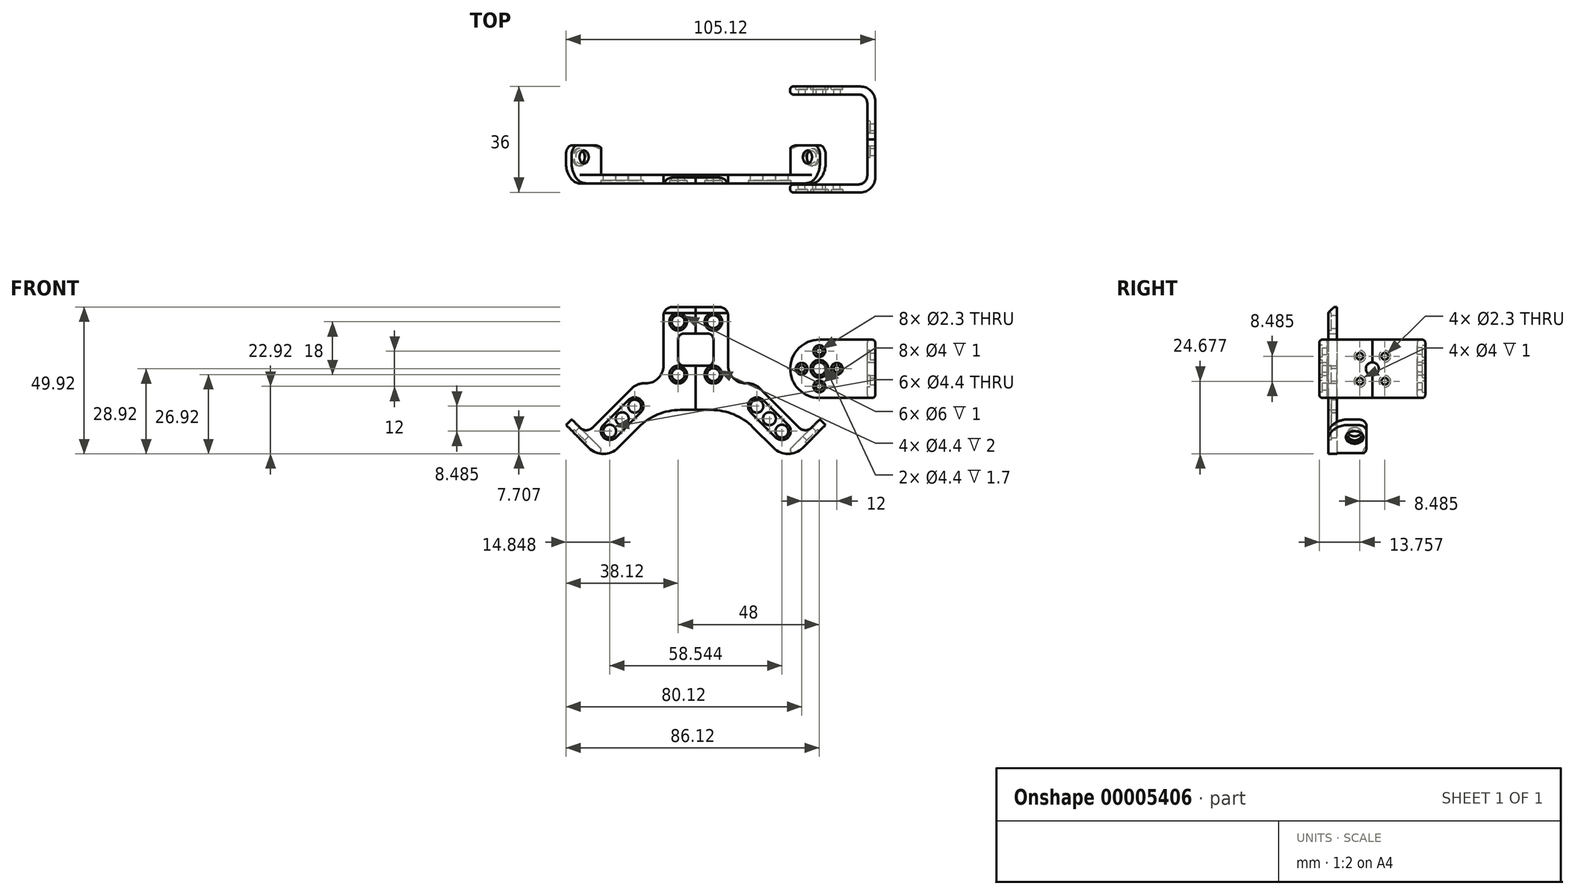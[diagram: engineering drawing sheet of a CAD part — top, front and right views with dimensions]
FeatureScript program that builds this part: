
annotation { "Feature Type Name" : "Feature", "Feature Type Description" : "" }
export const myFeature = defineFeature(function(context is Context, id is Id, definition is map)
    precondition{}
    {
        {
            var Q0;
            Q0=qCreatedBy(makeId("Front.planeOp"),FACE);
            var sketch = newSketch(context, id + "F0", { "sketchPlane" : qUnion([Q0])});
            skLineSegment(sketch, "E0", {"start": v(0, 210) * mm, "end": v(0, -40) * mm});
            skLineSegment(sketch, "E1", {"start": v(-61, 175) * mm, "end": v(61, 175) * mm});
            skPoint(sketch, "E2", {"position": v(0, 175) * mm});
            skLineSegment(sketch, "E3", {"start": v(0, 210) * mm, "end": v(0, 250) * mm});
            skLineSegment(sketch, "E4", {"start": v(-64.02, -38) * mm, "end": v(64.02, -38) * mm});
            skPoint(sketch, "E5", {"position": v(0, -38) * mm});
            skLineSegment(sketch, "E6", {"start": v(44.7, -38) * mm, "end": v(44.7, -100) * mm});
            skLineSegment(sketch, "E7", {"start": v(-51.1, 0) * mm, "end": v(47, 0) * mm});
            skSolve(sketch);
        }
        {
            var Q0;
            Q0=qCreatedBy(makeId("Front.planeOp"),FACE);
            var sketch = newSketch(context, id + "F1", { "sketchPlane" : qUnion([Q0])});
            skLineSegment(sketch, "E8.bottom", {"start": v(64, 184) * mm, "end": v(88, 184) * mm});
            skLineSegment(sketch, "E8.top", {"start": v(64, 148) * mm, "end": v(88, 148) * mm});
            skLineSegment(sketch, "E8.left", {"start": v(64, 184) * mm, "end": v(64, 148) * mm});
            skLineSegment(sketch, "E8.right", {"start": v(88, 184) * mm, "end": v(88, 148) * mm});
            skLineSegment(sketch, "E9", {"start": v(64, 183.9) * mm, "end": v(61, 183.9) * mm});
            skLineSegment(sketch, "E10", {"start": v(61, 183.9) * mm, "end": v(61, 166.1) * mm});
            skLineSegment(sketch, "E11", {"start": v(61, 166.1) * mm, "end": v(64, 166.1) * mm});
            skLineSegment(sketch, "E12", {"start": v(61, 175) * mm, "end": v(88, 175) * mm, "construction": true});
            skCircle(sketch, "E13", {"center": v(42, 175) * mm, "radius": 8.9 * mm});
            skLineSegment(sketch, "E14", {"start": v(14.42, 164.4) * mm, "end": v(39.88, 189.85) * mm});
            skLineSegment(sketch, "E15", {"start": v(39.88, 189.85) * mm, "end": v(56.85, 172.88) * mm});
            skLineSegment(sketch, "E16", {"start": v(56.85, 172.88) * mm, "end": v(31.4, 147.42) * mm});
            skLineSegment(sketch, "E17", {"start": v(31.4, 147.42) * mm, "end": v(14.42, 164.4) * mm});
            skLineSegment(sketch, "E18", {"start": v(33.51, 183.49) * mm, "end": v(50.49, 166.51) * mm, "construction": true});
            skLineSegment(sketch, "E19", {"start": v(48.36, 181.36) * mm, "end": v(22.9, 155.9) * mm, "construction": true});
            skLineSegment(sketch, "E20", {"start": v(2, 0) * mm, "end": v(2, 10) * mm});
            skLineSegment(sketch, "E21", {"start": v(2, 10) * mm, "end": v(5, 10) * mm});
            skLineSegment(sketch, "E22", {"start": v(5, 10) * mm, "end": v(5, 16) * mm});
            skLineSegment(sketch, "E23", {"start": v(5, 16) * mm, "end": v(10, 16) * mm});
            skLineSegment(sketch, "E24", {"start": v(10, 16) * mm, "end": v(10, 10) * mm});
            skLineSegment(sketch, "E25", {"start": v(10, 10) * mm, "end": v(21, 10) * mm});
            skLineSegment(sketch, "E26", {"start": v(21, 10) * mm, "end": v(21, 0) * mm, "construction": true});
            skLineSegment(sketch, "E27", {"start": v(21, 0) * mm, "end": v(2, 0) * mm, "construction": true});
            skLineSegment(sketch, "E28.0.MirrorCS", {"start": v(32, 10) * mm, "end": v(21, 10) * mm});
            skLineSegment(sketch, "E29.0.MirrorCS", {"start": v(32, 16) * mm, "end": v(32, 10) * mm});
            skLineSegment(sketch, "E30.0.MirrorCS", {"start": v(37, 16) * mm, "end": v(32, 16) * mm});
            skLineSegment(sketch, "E31.0.MirrorCS", {"start": v(37, 10) * mm, "end": v(37, 16) * mm});
            skLineSegment(sketch, "E32.0.MirrorCS", {"start": v(40, 10) * mm, "end": v(37, 10) * mm});
            skLineSegment(sketch, "E33.0.MirrorCS", {"start": v(40, 0) * mm, "end": v(40, 10) * mm});
            skLineSegment(sketch, "E34.0.MirrorCS", {"start": v(2, 0) * mm, "end": v(2, -10) * mm});
            skLineSegment(sketch, "E35.0.MirrorCS", {"start": v(2, -10) * mm, "end": v(5, -10) * mm});
            skLineSegment(sketch, "E36.0.MirrorCS", {"start": v(5, -10) * mm, "end": v(5, -16) * mm});
            skLineSegment(sketch, "E37.0.MirrorCS", {"start": v(5, -16) * mm, "end": v(10, -16) * mm});
            skLineSegment(sketch, "E38.0.MirrorCS", {"start": v(10, -16) * mm, "end": v(10, -10) * mm});
            skLineSegment(sketch, "E39.0.MirrorCS", {"start": v(10, -10) * mm, "end": v(21, -10) * mm});
            skLineSegment(sketch, "E40.0.MirrorCS", {"start": v(32, -10) * mm, "end": v(21, -10) * mm});
            skLineSegment(sketch, "E41.0.MirrorCS", {"start": v(32, -16) * mm, "end": v(32, -10) * mm});
            skLineSegment(sketch, "E42.0.MirrorCS", {"start": v(37, -16) * mm, "end": v(32, -16) * mm});
            skLineSegment(sketch, "E43.0.MirrorCS", {"start": v(37, -10) * mm, "end": v(37, -16) * mm});
            skLineSegment(sketch, "E44.0.MirrorCS", {"start": v(40, -10) * mm, "end": v(37, -10) * mm});
            skLineSegment(sketch, "E45.0.MirrorCS", {"start": v(40, 0) * mm, "end": v(40, -10) * mm});
            skLineSegment(sketch, "E46.0.MirrorCS", {"start": v(-2, -10) * mm, "end": v(-5, -10) * mm});
            skLineSegment(sketch, "E46.1.MirrorCS", {"start": v(-10, 10) * mm, "end": v(-21, 10) * mm});
            skLineSegment(sketch, "E46.2.MirrorCS", {"start": v(-32, -16) * mm, "end": v(-32, -10) * mm});
            skLineSegment(sketch, "E46.3.MirrorCS", {"start": v(-37, 10) * mm, "end": v(-37, 16) * mm});
            skLineSegment(sketch, "E46.4.MirrorCS", {"start": v(-5, -10) * mm, "end": v(-5, -16) * mm});
            skLineSegment(sketch, "E46.5.MirrorCS", {"start": v(-40, -10) * mm, "end": v(-37, -10) * mm});
            skLineSegment(sketch, "E46.6.MirrorCS", {"start": v(-32, 10) * mm, "end": v(-21, 10) * mm});
            skLineSegment(sketch, "E46.7.MirrorCS", {"start": v(-2, 0) * mm, "end": v(-2, 10) * mm});
            skLineSegment(sketch, "E46.8.MirrorCS", {"start": v(-10, -10) * mm, "end": v(-21, -10) * mm});
            skLineSegment(sketch, "E46.9.MirrorCS", {"start": v(-5, 16) * mm, "end": v(-10, 16) * mm});
            skLineSegment(sketch, "E46.10.MirrorCS", {"start": v(-5, 10) * mm, "end": v(-5, 16) * mm});
            skLineSegment(sketch, "E46.11.MirrorCS", {"start": v(-10, -16) * mm, "end": v(-10, -10) * mm});
            skLineSegment(sketch, "E46.12.MirrorCS", {"start": v(-37, -10) * mm, "end": v(-37, -16) * mm});
            skLineSegment(sketch, "E46.13.MirrorCS", {"start": v(-40, 0) * mm, "end": v(-40, 10) * mm});
            skLineSegment(sketch, "E46.14.MirrorCS", {"start": v(-40, 10) * mm, "end": v(-37, 10) * mm});
            skLineSegment(sketch, "E46.15.MirrorCS", {"start": v(-21, 0) * mm, "end": v(-2, 0) * mm, "construction": true});
            skLineSegment(sketch, "E46.16.MirrorCS", {"start": v(-10, 16) * mm, "end": v(-10, 10) * mm});
            skLineSegment(sketch, "E46.17.MirrorCS", {"start": v(-2, 0) * mm, "end": v(-2, -10) * mm});
            skLineSegment(sketch, "E46.18.MirrorCS", {"start": v(-32, -10) * mm, "end": v(-21, -10) * mm});
            skLineSegment(sketch, "E46.19.MirrorCS", {"start": v(-37, -16) * mm, "end": v(-32, -16) * mm});
            skLineSegment(sketch, "E46.20.MirrorCS", {"start": v(-37, 16) * mm, "end": v(-32, 16) * mm});
            skLineSegment(sketch, "E46.21.MirrorCS", {"start": v(-2, 10) * mm, "end": v(-5, 10) * mm});
            skLineSegment(sketch, "E46.22.MirrorCS", {"start": v(-5, -16) * mm, "end": v(-10, -16) * mm});
            skLineSegment(sketch, "E46.23.MirrorCS", {"start": v(-32, 16) * mm, "end": v(-32, 10) * mm});
            skLineSegment(sketch, "E46.24.MirrorCS", {"start": v(-40, 0) * mm, "end": v(-40, -10) * mm});
            skLineSegment(sketch, "E46.25.MirrorCS", {"start": v(-21, 10) * mm, "end": v(-21, 0) * mm, "construction": true});
            skLineSegment(sketch, "E47.rect.bottom", {"start": v(42.5, 26.5) * mm, "end": v(-42.5, 26.5) * mm});
            skLineSegment(sketch, "E47.rect.top", {"start": v(42.5, 63.5) * mm, "end": v(-42.5, 63.5) * mm});
            skLineSegment(sketch, "E47.rect.left", {"start": v(42.5, 26.5) * mm, "end": v(42.5, 63.5) * mm});
            skLineSegment(sketch, "E47.rect.right", {"start": v(-42.5, 26.5) * mm, "end": v(-42.5, 63.5) * mm});
            skPoint(sketch, "E47.rect.middle", {"position": v(0, 45) * mm});
            skLineSegment(sketch, "E48.rect.bottom", {"start": v(12, 213) * mm, "end": v(-12, 213) * mm});
            skLineSegment(sketch, "E48.rect.top", {"start": v(12, 237) * mm, "end": v(-12, 237) * mm});
            skLineSegment(sketch, "E48.rect.left", {"start": v(12, 213) * mm, "end": v(12, 237) * mm});
            skLineSegment(sketch, "E48.rect.right", {"start": v(-12, 213) * mm, "end": v(-12, 237) * mm});
            skPoint(sketch, "E48.rect.middle", {"position": v(0, 225) * mm});
            skLineSegment(sketch, "E49", {"start": v(-8.9, 213) * mm, "end": v(-8.9, 210) * mm});
            skLineSegment(sketch, "E50", {"start": v(-8.9, 210) * mm, "end": v(8.9, 210) * mm});
            skLineSegment(sketch, "E51", {"start": v(8.9, 210) * mm, "end": v(8.9, 213) * mm});
            skLineSegment(sketch, "E52.rect.bottom", {"start": v(-12, 200) * mm, "end": v(12, 200) * mm});
            skLineSegment(sketch, "E52.rect.top", {"start": v(-12, 164) * mm, "end": v(12, 164) * mm});
            skLineSegment(sketch, "E52.rect.left", {"start": v(-12, 200) * mm, "end": v(-12, 164) * mm});
            skLineSegment(sketch, "E52.rect.right", {"start": v(12, 200) * mm, "end": v(12, 164) * mm});
            skPoint(sketch, "E52.rect.middle", {"position": v(0, 182) * mm});
            skLineSegment(sketch, "E53.rect.bottom", {"start": v(15, 182.1) * mm, "end": v(-15, 182.1) * mm});
            skLineSegment(sketch, "E53.rect.top", {"start": v(15, 199.9) * mm, "end": v(-15, 199.9) * mm});
            skLineSegment(sketch, "E53.rect.left", {"start": v(15, 182.1) * mm, "end": v(15, 199.9) * mm});
            skLineSegment(sketch, "E53.rect.right", {"start": v(-15, 182.1) * mm, "end": v(-15, 199.9) * mm});
            skPoint(sketch, "E53.rect.middle", {"position": v(0, 191) * mm});
            skCircle(sketch, "E54", {"center": v(42, 175) * mm, "radius": 15 * mm, "construction": true});
            skCircle(sketch, "E55", {"center": v(42, 175) * mm, "radius": 6 * mm, "construction": true});
            skCircle(sketch, "E56", {"center": v(46.24, 179.24) * mm, "radius": 2.5 * mm, "construction": true});
            skCircle(sketch, "E57", {"center": v(37.76, 179.24) * mm, "radius": 2.5 * mm, "construction": true});
            skCircle(sketch, "E58", {"center": v(37.76, 170.76) * mm, "radius": 2.5 * mm, "construction": true});
            skCircle(sketch, "E59", {"center": v(46.24, 170.76) * mm, "radius": 2.5 * mm, "construction": true});
            skLineSegment(sketch, "E60", {"start": v(42, 181) * mm, "end": v(42, 169) * mm, "construction": true});
            skLineSegment(sketch, "E61", {"start": v(48, 175) * mm, "end": v(36, 175) * mm, "construction": true});
            skCircle(sketch, "E62", {"center": v(42, 181) * mm, "radius": 0.8 * mm});
            skCircle(sketch, "E63", {"center": v(48, 175) * mm, "radius": 0.8 * mm});
            skCircle(sketch, "E64", {"center": v(42, 169) * mm, "radius": 0.8 * mm});
            skCircle(sketch, "E65", {"center": v(36, 175) * mm, "radius": 0.8 * mm});
            skLineSegment(sketch, "E66", {"start": v(-6, 191) * mm, "end": v(6, 191) * mm, "construction": true});
            skLineSegment(sketch, "E67", {"start": v(-6, 173) * mm, "end": v(6, 173) * mm, "construction": true});
            skCircle(sketch, "E68", {"center": v(-6, 191) * mm, "radius": 2.5 * mm});
            skCircle(sketch, "E69", {"center": v(0, 191) * mm, "radius": 2.5 * mm});
            skCircle(sketch, "E70", {"center": v(6, 191) * mm, "radius": 2.5 * mm});
            skCircle(sketch, "E71", {"center": v(-6, 173) * mm, "radius": 2.5 * mm});
            skCircle(sketch, "E72", {"center": v(0, 173) * mm, "radius": 2.5 * mm});
            skCircle(sketch, "E73", {"center": v(6, 173) * mm, "radius": 2.5 * mm});
            skLineSegment(sketch, "E74", {"start": v(20.79, 162.27) * mm, "end": v(29.27, 153.79) * mm, "construction": true});
            skCircle(sketch, "E75", {"center": v(29.27, 153.79) * mm, "radius": 2.5 * mm, "construction": true});
            skCircle(sketch, "E76", {"center": v(20.79, 162.27) * mm, "radius": 2.5 * mm, "construction": true});
            skCircle(sketch, "E77", {"center": v(25.03, 158.03) * mm, "radius": 2.5 * mm, "construction": true});
            skLineSegment(sketch, "E78.rect.bottom", {"start": v(12, 81.5) * mm, "end": v(-12, 81.5) * mm});
            skLineSegment(sketch, "E78.rect.top", {"start": v(12, 105.5) * mm, "end": v(-12, 105.5) * mm});
            skLineSegment(sketch, "E78.rect.left", {"start": v(12, 81.5) * mm, "end": v(12, 105.5) * mm});
            skLineSegment(sketch, "E78.rect.right", {"start": v(-12, 81.5) * mm, "end": v(-12, 105.5) * mm});
            skPoint(sketch, "E78.rect.middle", {"position": v(0, 93.5) * mm});
            skLineSegment(sketch, "E79", {"start": v(-8.9, 81.5) * mm, "end": v(-8.9, 78.5) * mm});
            skLineSegment(sketch, "E80", {"start": v(-8.9, 78.5) * mm, "end": v(8.9, 78.5) * mm});
            skLineSegment(sketch, "E81", {"start": v(8.9, 78.5) * mm, "end": v(8.9, 81.5) * mm});
            skLineSegment(sketch, "E82", {"start": v(0, 93.5) * mm, "end": v(0, 78.5) * mm, "construction": true});
            skCircle(sketch, "E83", {"center": v(42, 175) * mm, "radius": 2.5 * mm});
            skSolve(sketch);
        }
        {
            var Q0;
            Q0=qCreatedBy(makeId("Front.planeOp"),FACE);
            var sketch = newSketch(context, id + "F2", { "sketchPlane" : qUnion([Q0])});
            skArc(sketch, "E84", {"start": v(42, 184.9) * mm, "mid": v(32.1, 175) * mm, "end": v(42, 165.1) * mm});
            skLineSegment(sketch, "E85", {"start": v(61, 184.9) * mm, "end": v(61, 165.1) * mm});
            skLineSegment(sketch, "E86", {"start": v(61, 165.1) * mm, "end": v(42, 165.1) * mm});
            skLineSegment(sketch, "E87", {"start": v(61, 184.9) * mm, "end": v(42, 184.9) * mm});
            skCircle(sketch, "E88", {"center": v(42, 181) * mm, "radius": 1.15 * mm});
            skCircle(sketch, "E89", {"center": v(48, 175) * mm, "radius": 1.15 * mm});
            skCircle(sketch, "E90", {"center": v(42, 169) * mm, "radius": 1.15 * mm});
            skCircle(sketch, "E91", {"center": v(36, 175) * mm, "radius": 1.15 * mm});
            skCircle(sketch, "E92", {"center": v(42, 175) * mm, "radius": 2.2 * mm});
            skSolve(sketch);
        }
        {
            var Q0;
            Q0=qCreatedBy(makeId("Top.planeOp"),FACE);
            var Q1;
            Q1=sQuery(id+"F0.wireOp",VERTEX,"E2");
            cPlane(context, id + "F3", {"entities" : qUnion([Q0, Q1]), "cplaneType" : CPlaneType.PLANE_POINT, "offset" : 150 * mm, "width" : 150 * mm, "height" : 150 * mm});
        }
        {
            var Q0;
            Q0=makeQuery(id+"F2.imprint","IMPRINT",FACE,{"disambiguationData":[TD([[makeQuery(id+"F2.imprint","IMPRINT",EDGE,{"derivedFrom":sQuery(id+"F2.wireOp",EDGE,"E84")}),1.0]])]});
            extrude(context, id + "F4", {"entities" : qUnion([Q0]), "depth" : 18 * mm});
        }
        {
            var Q0;
            Q0=qCreatedBy(id+"F3.planeOp",FACE);
            var sketch = newSketch(context, id + "F5", { "sketchPlane" : qUnion([Q0])});
            skLineSegment(sketch, "E93.bottom", {"start": v(27, 0) * mm, "end": v(58.3, 0) * mm});
            skLineSegment(sketch, "E93.top", {"start": v(27, -15.3) * mm, "end": v(55.3, -15.3) * mm});
            skLineSegment(sketch, "E93.left", {"start": v(27, 0) * mm, "end": v(27, -15.3) * mm});
            skLineSegment(sketch, "E93.right", {"start": v(58.3, 0) * mm, "end": v(58.3, -12.3) * mm});
            skPoint(sketch, "E94.visualSharp", {"position": v(58.3, -15.3) * mm});
            skArc(sketch, "E94.filletArc", {"start": v(55.3, -15.3) * mm, "mid": v(57.42, -14.42) * mm, "end": v(58.3, -12.3) * mm});
            skSolve(sketch);
        }
        {
            var Q0;
            Q0=makeQuery(id+"F5.imprint","IMPRINT",FACE,{"disambiguationData":[TD([[makeQuery(id+"F5.imprint","IMPRINT",EDGE,{"derivedFrom":sQuery(id+"F5.wireOp",EDGE,"E93.bottom")}),-1.0]])]});
            extrude(context, id + "F6", {"entities" : qUnion([Q0]), "operationType" : NewBodyOperationType.REMOVE, "endBound" : BoundingType.SYMMETRIC, "oppositeDirection" : true, "depth" : 25 * mm});
        }
        {
            var Q0;
            Q0=makeQuery(id+"F4.opExtrude","SWEPT_FACE",FACE,{"disambiguationData":[OSD([sQuery(id+"F2.wireOp",EDGE,"E85")])]});
            var sketch = newSketch(context, id + "F7", { "sketchPlane" : qUnion([Q0])});
            skCircle(sketch, "E95", {"center": v(0, 175) * mm, "radius": 8.9 * mm});
            skCircle(sketch, "E96", {"center": v(0, 175) * mm, "radius": 6 * mm, "construction": true});
            skCircle(sketch, "E97", {"center": v(0, 181) * mm, "radius": 2.5 * mm});
            skCircle(sketch, "E98", {"center": v(-6, 175) * mm, "radius": 2.5 * mm});
            skCircle(sketch, "E99", {"center": v(0, 169) * mm, "radius": 2.5 * mm});
            skCircle(sketch, "E100", {"center": v(6, 175) * mm, "radius": 2.5 * mm});
            skLineSegment(sketch, "E101", {"start": v(-4.24, 179.24) * mm, "end": v(4.24, 170.76) * mm, "construction": true});
            skLineSegment(sketch, "E102", {"start": v(4.24, 179.24) * mm, "end": v(-4.24, 170.76) * mm, "construction": true});
            skCircle(sketch, "E103", {"center": v(-4.24, 179.24) * mm, "radius": 0.8 * mm});
            skCircle(sketch, "E104", {"center": v(4.24, 179.24) * mm, "radius": 0.8 * mm});
            skCircle(sketch, "E105", {"center": v(4.24, 170.76) * mm, "radius": 0.8 * mm});
            skCircle(sketch, "E106", {"center": v(-4.24, 170.76) * mm, "radius": 0.8 * mm});
            skLineSegment(sketch, "E107", {"start": v(0, 181) * mm, "end": v(0, 169) * mm, "construction": true});
            skCircle(sketch, "E108", {"center": v(0, 175) * mm, "radius": 2.5 * mm});
            skSolve(sketch);
        }
        {
            var Q0;
            {var subQ0=sQuery(id+"F2.wireOp",EDGE,"E85");Q0=makeQuery(id+"F7.imprint","IMPRINT",FACE,{"disambiguationData":[TD([[makeQuery(id+"F7.imprint","IMPRINT",EDGE,{"derivedFrom":makeQuery(id+"F4.opExtrude","CAP_EDGE",EDGE,{"disambiguationData":[OSD([subQ0])],"isStart":false})}),1.0]])]});}
            var sketch = newSketch(context, id + "F8", { "sketchPlane" : qUnion([Q0])});
            skCircle(sketch, "E109", {"center": v(-4.24, 179.24) * mm, "radius": 1.15 * mm});
            skCircle(sketch, "E110", {"center": v(-4.24, 170.76) * mm, "radius": 1.15 * mm});
            skCircle(sketch, "E111", {"center": v(0, 175) * mm, "radius": 2.2 * mm});
            skSolve(sketch);
        }
        {
            var Q0;
            {Q0=qUnion([makeQuery(id+"F8.imprint","IMPRINT",FACE,{"disambiguationData":[TD([[makeQuery(id+"F8.imprint","IMPRINT",EDGE,{"derivedFrom":sQuery(id+"F8.wireOp",EDGE,"E109")}),1.0]])]}),makeQuery(id+"F8.imprint","IMPRINT",FACE,{"disambiguationData":[TD([[makeQuery(id+"F8.imprint","IMPRINT",EDGE,{"derivedFrom":sQuery(id+"F8.wireOp",EDGE,"E110")}),1.0]])]}),makeQuery(id+"F8.imprint","IMPRINT",FACE,{"disambiguationData":[TD([[makeQuery(id+"F8.imprint","IMPRINT",EDGE,{"derivedFrom":sQuery(id+"F8.wireOp",EDGE,"E111")}),1.0]])]})]);}
            extrude(context, id + "F9", {"entities" : qUnion([Q0]), "operationType" : NewBodyOperationType.REMOVE, "endBound" : BoundingType.UP_TO_NEXT, "oppositeDirection" : true, "depth" : 25 * mm});
        }
        {
            var Q0;
            Q0=makeQuery(id+"F6.boolean.opBoolean","COPY",FACE,{"derivedFrom":makeQuery(id+"F6.opExtrude","SWEPT_FACE",FACE,{"disambiguationData":[OSD([sQuery(id+"F5.wireOp",EDGE,"E93.right")])]})});
            var sketch = newSketch(context, id + "F10", { "sketchPlane" : qUnion([Q0])});
            skCircle(sketch, "E112", {"center": v(0, 175) * mm, "radius": 3 * mm});
            skCircle(sketch, "E113", {"center": v(4.24, 179.24) * mm, "radius": 2 * mm});
            skCircle(sketch, "E114", {"center": v(4.24, 170.76) * mm, "radius": 2 * mm});
            skSolve(sketch);
        }
        {
            var Q0;
            {var subQ4=sQuery(id+"F5.wireOp",EDGE,"E93.right");var subQ5=makeQuery(id+"F6.boolean.opBoolean","COPY",FACE,{"derivedFrom":makeQuery(id+"F6.opExtrude","SWEPT_FACE",FACE,{"disambiguationData":[OSD([subQ4])]})});var subQ6=sQuery(id+"F8.wireOp",EDGE,"E111");var subQ13=makeQuery(id+"F9.boolean.opBoolean","COPY",EDGE,{"derivedFrom":makeQuery(id+"F9.opExtrude","CAP_EDGE",EDGE,{"disambiguationData":[OSD([subQ6]),topologyDisambiguationEdgeConnected([subQ5])],"isStart":false})});var subQ15=makeQuery(id+"F10.imprint","IMPRINT",EDGE,{"derivedFrom":subQ13});var subQ17=makeQuery(id+"F10.imprint","IMPRINT",EDGE,{"derivedFrom":makeQuery(id+"F9.boolean.opBoolean","COPY",EDGE,{"derivedFrom":makeQuery(id+"F9.opExtrude","CAP_EDGE",EDGE,{"disambiguationData":[OSD([sQuery(id+"F8.wireOp",EDGE,"E110")])],"isStart":false})})});var subQ18=makeQuery(id+"F10.imprint","IMPRINT",EDGE,{"derivedFrom":makeQuery(id+"F9.boolean.opBoolean","COPY",EDGE,{"derivedFrom":makeQuery(id+"F9.opExtrude","CAP_EDGE",EDGE,{"disambiguationData":[OSD([sQuery(id+"F8.wireOp",EDGE,"E109")])],"isStart":false})})});Q0=qUnion([makeQuery(id+"F10.imprint","IMPRINT",FACE,{"disambiguationData":[TD([[subQ18,-1.0]])]}),makeQuery(id+"F10.imprint","IMPRINT",FACE,{"disambiguationData":[TD([[subQ17,-1.0]])]}),makeQuery(id+"F10.imprint","IMPRINT",FACE,{"disambiguationData":[TD([[makeQuery(id+"F10.imprint","IMPRINT",EDGE,{"derivedFrom":sQuery(id+"F10.wireOp",EDGE,"E113")}),1.0]])]}),makeQuery(id+"F10.imprint","IMPRINT",FACE,{"disambiguationData":[TD([[makeQuery(id+"F10.imprint","IMPRINT",EDGE,{"derivedFrom":sQuery(id+"F10.wireOp",EDGE,"E114")}),1.0]])]}),makeQuery(id+"F10.imprint","IMPRINT",FACE,{"disambiguationData":[TD([[subQ15,-1.0]])]}),makeQuery(id+"F10.imprint","IMPRINT",FACE,{"disambiguationData":[TD([[subQ15,1.0]])]})]);}
            extrude(context, id + "F11", {"entities" : qUnion([Q0]), "operationType" : NewBodyOperationType.REMOVE, "oppositeDirection" : true, "depth" : 1 * mm});
        }
        {
            var Q0;
            Q0=makeQuery(id+"F4.opExtrude","CAP_FACE",FACE,{"disambiguationData":[OSD([sQuery(id+"F2.wireOp",EDGE,"E84"),sQuery(id+"F2.wireOp",EDGE,"E85"),sQuery(id+"F2.wireOp",EDGE,"E86"),sQuery(id+"F2.wireOp",EDGE,"E87"),sQuery(id+"F2.wireOp",EDGE,"E88"),sQuery(id+"F2.wireOp",EDGE,"E89"),sQuery(id+"F2.wireOp",EDGE,"E90"),sQuery(id+"F2.wireOp",EDGE,"E91"),sQuery(id+"F2.wireOp",EDGE,"E92")])],"isStart":false});
            var sketch = newSketch(context, id + "F12", { "sketchPlane" : qUnion([Q0])});
            skCircle(sketch, "E115", {"center": v(36, 175) * mm, "radius": 2 * mm});
            skCircle(sketch, "E116", {"center": v(42, 181) * mm, "radius": 2 * mm});
            skCircle(sketch, "E117", {"center": v(42, 175) * mm, "radius": 3 * mm});
            skCircle(sketch, "E118", {"center": v(48, 175) * mm, "radius": 2 * mm});
            skCircle(sketch, "E119", {"center": v(42, 169) * mm, "radius": 2 * mm});
            skSolve(sketch);
        }
        {
            var Q0;
            {var subQ0=makeQuery(id+"F12.imprint","IMPRINT",EDGE,{"derivedFrom":makeQuery(id+"F4.opExtrude","CAP_EDGE",EDGE,{"disambiguationData":[OSD([sQuery(id+"F2.wireOp",EDGE,"E88")])],"isStart":false})});var subQ1=makeQuery(id+"F12.imprint","IMPRINT",EDGE,{"derivedFrom":makeQuery(id+"F4.opExtrude","CAP_EDGE",EDGE,{"disambiguationData":[OSD([sQuery(id+"F2.wireOp",EDGE,"E89")])],"isStart":false})});var subQ2=makeQuery(id+"F12.imprint","IMPRINT",EDGE,{"derivedFrom":makeQuery(id+"F4.opExtrude","CAP_EDGE",EDGE,{"disambiguationData":[OSD([sQuery(id+"F2.wireOp",EDGE,"E90")])],"isStart":false})});var subQ3=makeQuery(id+"F12.imprint","IMPRINT",EDGE,{"derivedFrom":makeQuery(id+"F4.opExtrude","CAP_EDGE",EDGE,{"disambiguationData":[OSD([sQuery(id+"F2.wireOp",EDGE,"E91")])],"isStart":false})});var subQ4=makeQuery(id+"F12.imprint","IMPRINT",EDGE,{"derivedFrom":makeQuery(id+"F4.opExtrude","CAP_EDGE",EDGE,{"disambiguationData":[OSD([sQuery(id+"F2.wireOp",EDGE,"E92")])],"isStart":false})});Q0=qUnion([makeQuery(id+"F12.imprint","IMPRINT",FACE,{"disambiguationData":[TD([[subQ0,1.0]])]}),makeQuery(id+"F12.imprint","IMPRINT",FACE,{"disambiguationData":[TD([[subQ1,1.0]])]}),makeQuery(id+"F12.imprint","IMPRINT",FACE,{"disambiguationData":[TD([[subQ2,1.0]])]}),makeQuery(id+"F12.imprint","IMPRINT",FACE,{"disambiguationData":[TD([[subQ3,1.0]])]}),makeQuery(id+"F12.imprint","IMPRINT",FACE,{"disambiguationData":[TD([[subQ4,1.0]])]}),makeQuery(id+"F12.imprint","IMPRINT",FACE,{"disambiguationData":[TD([[makeQuery(id+"F12.imprint","IMPRINT",EDGE,{"derivedFrom":sQuery(id+"F12.wireOp",EDGE,"E115")}),1.0]])]}),makeQuery(id+"F12.imprint","IMPRINT",FACE,{"disambiguationData":[TD([[makeQuery(id+"F12.imprint","IMPRINT",EDGE,{"derivedFrom":sQuery(id+"F12.wireOp",EDGE,"E116")}),1.0]])]}),makeQuery(id+"F12.imprint","IMPRINT",FACE,{"disambiguationData":[TD([[makeQuery(id+"F12.imprint","IMPRINT",EDGE,{"derivedFrom":sQuery(id+"F12.wireOp",EDGE,"E117")}),1.0]])]}),makeQuery(id+"F12.imprint","IMPRINT",FACE,{"disambiguationData":[TD([[makeQuery(id+"F12.imprint","IMPRINT",EDGE,{"derivedFrom":sQuery(id+"F12.wireOp",EDGE,"E118")}),1.0]])]}),makeQuery(id+"F12.imprint","IMPRINT",FACE,{"disambiguationData":[TD([[makeQuery(id+"F12.imprint","IMPRINT",EDGE,{"derivedFrom":sQuery(id+"F12.wireOp",EDGE,"E119")}),1.0]])]})]);}
            extrude(context, id + "F13", {"entities" : qUnion([Q0]), "operationType" : NewBodyOperationType.REMOVE, "oppositeDirection" : true, "depth" : 1 * mm});
        }
        {
            var Q0;
            Q0=makeQuery(id+"F4.opExtrude","CAP_EDGE",EDGE,{"disambiguationData":[OSD([sQuery(id+"F2.wireOp",EDGE,"E85")])],"isStart":false});
            fillet(context, id + "F14", {"entities" : qUnion([Q0]), "radius" : 5 * mm, "tangentPropagation" : true, "allowEdgeOverflow" : false});
        }
        {
            var Q0;
            Q0=makeQuery(id+"F4.opExtrude","CAP_EDGE",EDGE,{"disambiguationData":[OSD([sQuery(id+"F2.wireOp",EDGE,"E84")])],"isStart":false});
            var Q1;
            Q1=makeQuery(id+"F6.boolean.opBoolean","INTERSECT",EDGE,{"derivedFrom":[makeQuery(id+"F4.opExtrude","SWEPT_FACE",FACE,{"disambiguationData":[OSD([sQuery(id+"F2.wireOp",EDGE,"E84")])]}),makeQuery(id+"F6.opExtrude","SWEPT_FACE",FACE,{"disambiguationData":[OSD([sQuery(id+"F5.wireOp",EDGE,"E93.top")])]})]});
            fillet(context, id + "F15", {"entities" : qUnion([Q0, Q1]), "radius" : 1 * mm, "tangentPropagation" : true, "allowEdgeOverflow" : false});
        }
        {
            var Q0;
            {var subQ0=sQuery(id+"F2.wireOp",EDGE,"E85");var subQ2=sQuery(id+"F2.wireOp",EDGE,"E86");var subQ5=sQuery(id+"F2.wireOp",EDGE,"E87");var subQ6=makeQuery(id+"F4.opExtrude","CAP_FACE",FACE,{"disambiguationData":[OSD([sQuery(id+"F2.wireOp",EDGE,"E84"),subQ0,subQ2,subQ5,sQuery(id+"F2.wireOp",EDGE,"E88"),sQuery(id+"F2.wireOp",EDGE,"E89"),sQuery(id+"F2.wireOp",EDGE,"E90"),sQuery(id+"F2.wireOp",EDGE,"E91"),sQuery(id+"F2.wireOp",EDGE,"E92")])],"isStart":true});Q0=qUnion([makeQuery(id+"F9.boolean.opBoolean","SPLIT",FACE,{"disambiguationData":[TD([makeQuery(id+"F4.opExtrude","SWEPT_FACE",FACE,{"disambiguationData":[OSD([subQ5])]})])],"derivedFrom":subQ6}),makeQuery(id+"F9.boolean.opBoolean","SPLIT",FACE,{"disambiguationData":[TD([makeQuery(id+"F4.opExtrude","SWEPT_FACE",FACE,{"disambiguationData":[OSD([subQ2])]})])],"derivedFrom":subQ6})]);}
            var Q1;
            Q1=makeQuery(id+"F4.opExtrude","SWEPT_BODY",BODY,{"disambiguationData":[OSD([sQuery(id+"F2.wireOp",EDGE,"E84"),sQuery(id+"F2.wireOp",EDGE,"E85"),sQuery(id+"F2.wireOp",EDGE,"E86"),sQuery(id+"F2.wireOp",EDGE,"E87"),sQuery(id+"F2.wireOp",EDGE,"E88"),sQuery(id+"F2.wireOp",EDGE,"E89"),sQuery(id+"F2.wireOp",EDGE,"E90"),sQuery(id+"F2.wireOp",EDGE,"E91"),sQuery(id+"F2.wireOp",EDGE,"E92")])]});
            var Q2;
            {var subQ0=sQuery(id+"F2.wireOp",EDGE,"E85");var subQ2=sQuery(id+"F2.wireOp",EDGE,"E86");var subQ5=sQuery(id+"F2.wireOp",EDGE,"E87");var subQ6=makeQuery(id+"F4.opExtrude","CAP_FACE",FACE,{"disambiguationData":[OSD([sQuery(id+"F2.wireOp",EDGE,"E84"),subQ0,subQ2,subQ5,sQuery(id+"F2.wireOp",EDGE,"E88"),sQuery(id+"F2.wireOp",EDGE,"E89"),sQuery(id+"F2.wireOp",EDGE,"E90"),sQuery(id+"F2.wireOp",EDGE,"E91"),sQuery(id+"F2.wireOp",EDGE,"E92")])],"isStart":true});Q2=qUnion([makeQuery(id+"F9.boolean.opBoolean","SPLIT",FACE,{"disambiguationData":[TD([makeQuery(id+"F4.opExtrude","SWEPT_FACE",FACE,{"disambiguationData":[OSD([subQ5])]})])],"derivedFrom":subQ6}),makeQuery(id+"F9.boolean.opBoolean","SPLIT",FACE,{"disambiguationData":[TD([makeQuery(id+"F4.opExtrude","SWEPT_FACE",FACE,{"disambiguationData":[OSD([subQ2])]})])],"derivedFrom":subQ6})]);}
            mirror(context, id + "F16", {"faces" : qUnion([Q0]), "entities" : qUnion([Q1]), "mirrorPlane" : qUnion([Q2])});
        }
        {
            var Q0;
            Q0=qCreatedBy(makeId("Front.planeOp"),FACE);
            cPlane(context, id + "F17", {"entities" : qUnion([Q0]), "cplaneType" : CPlaneType.OFFSET, "offset" : 12 * mm, "width" : 150 * mm, "height" : 150 * mm});
        }
        {
            var Q0;
            Q0=qCreatedBy(id+"F17.planeOp",FACE);
            var sketch = newSketch(context, id + "F18", { "sketchPlane" : qUnion([Q0])});
            skLineSegment(sketch, "E120", {"start": v(0, 196) * mm, "end": v(8, 196) * mm});
            skLineSegment(sketch, "E121", {"start": v(21.84, 168.3) * mm, "end": v(37.26, 152.87) * mm});
            skLineSegment(sketch, "E122", {"start": v(5.29, 161) * mm, "end": v(0, 161) * mm});
            skLineSegment(sketch, "E123", {"start": v(0, 161) * mm, "end": v(0, 176) * mm});
            skLineSegment(sketch, "E124", {"start": v(20.79, 170.76) * mm, "end": v(37.76, 153.79) * mm, "construction": true});
            skLineSegment(sketch, "E125", {"start": v(37.26, 152.87) * mm, "end": v(42.21, 157.82) * mm});
            skLineSegment(sketch, "E126", {"start": v(42.21, 157.82) * mm, "end": v(44.12, 155.9) * mm});
            skLineSegment(sketch, "E127", {"start": v(44.12, 155.9) * mm, "end": v(31.4, 143.18) * mm});
            skLineSegment(sketch, "E128", {"start": v(11, 193) * mm, "end": v(11, 176.05) * mm});
            skLineSegment(sketch, "E129", {"start": v(19.43, 155.14) * mm, "end": v(31.4, 143.18) * mm});
            skCircle(sketch, "E130", {"center": v(6, 191) * mm, "radius": 2.2 * mm});
            skCircle(sketch, "E131", {"center": v(6, 173) * mm, "radius": 2.2 * mm});
            skCircle(sketch, "E132", {"center": v(20.79, 162.27) * mm, "radius": 2.2 * mm});
            skCircle(sketch, "E133", {"center": v(25.03, 158.03) * mm, "radius": 2.2 * mm});
            skCircle(sketch, "E134", {"center": v(29.27, 153.79) * mm, "radius": 2.2 * mm});
            skLineSegment(sketch, "E135", {"start": v(17.6, 170.05) * mm, "end": v(17, 170.05) * mm});
            skPoint(sketch, "E136.visualSharp", {"position": v(11, 170.05) * mm});
            skArc(sketch, "E136.filletArc", {"start": v(11, 176.05) * mm, "mid": v(12.76, 171.8) * mm, "end": v(17, 170.05) * mm});
            skPoint(sketch, "E137.visualSharp", {"position": v(20.08, 170.05) * mm});
            skArc(sketch, "E137.filletArc", {"start": v(21.84, 168.3) * mm, "mid": v(19.9, 169.6) * mm, "end": v(17.6, 170.05) * mm});
            skPoint(sketch, "E138.visualSharp", {"position": v(13.57, 161) * mm});
            skArc(sketch, "E138.filletArc", {"start": v(19.43, 155.14) * mm, "mid": v(12.94, 159.48) * mm, "end": v(5.29, 161) * mm});
            skPoint(sketch, "E139.visualSharp", {"position": v(11, 196) * mm});
            skArc(sketch, "E139.filletArc", {"start": v(11, 193) * mm, "mid": v(10.12, 195.12) * mm, "end": v(8, 196) * mm});
            skLineSegment(sketch, "E140", {"start": v(0, 187) * mm, "end": v(4, 187) * mm});
            skLineSegment(sketch, "E141", {"start": v(6, 185) * mm, "end": v(6, 178) * mm});
            skLineSegment(sketch, "E142", {"start": v(4, 176) * mm, "end": v(0, 176) * mm});
            skLineSegment(sketch, "E143.trimOffspring", {"start": v(0, 187) * mm, "end": v(0, 196) * mm});
            skPoint(sketch, "E144.visualSharp", {"position": v(6, 187) * mm});
            skArc(sketch, "E144.filletArc", {"start": v(6, 185) * mm, "mid": v(5.41, 186.41) * mm, "end": v(4, 187) * mm});
            skPoint(sketch, "E145.visualSharp", {"position": v(6, 176) * mm});
            skArc(sketch, "E145.filletArc", {"start": v(4, 176) * mm, "mid": v(5.41, 176.59) * mm, "end": v(6, 178) * mm});
            skSolve(sketch);
        }
        {
            var Q0;
            Q0=makeQuery(id+"F18.imprint","IMPRINT",FACE,{"disambiguationData":[TD([[makeQuery(id+"F18.imprint","IMPRINT",EDGE,{"derivedFrom":sQuery(id+"F18.wireOp",EDGE,"E120")}),-1.0]])]});
            extrude(context, id + "F19", {"entities" : qUnion([Q0]), "depth" : 3 * mm});
        }
        {
            var Q0;
            Q0=makeQuery(id+"F19.opExtrude","CAP_FACE",FACE,{"disambiguationData":[OSD([sQuery(id+"F18.wireOp",EDGE,"E120"),sQuery(id+"F18.wireOp",EDGE,"E121"),sQuery(id+"F18.wireOp",EDGE,"E122"),sQuery(id+"F18.wireOp",EDGE,"E123"),sQuery(id+"F18.wireOp",EDGE,"E125"),sQuery(id+"F18.wireOp",EDGE,"E126"),sQuery(id+"F18.wireOp",EDGE,"E127"),sQuery(id+"F18.wireOp",EDGE,"E128"),sQuery(id+"F18.wireOp",EDGE,"E129"),sQuery(id+"F18.wireOp",EDGE,"E130"),sQuery(id+"F18.wireOp",EDGE,"E131"),sQuery(id+"F18.wireOp",EDGE,"E132"),sQuery(id+"F18.wireOp",EDGE,"E133"),sQuery(id+"F18.wireOp",EDGE,"E134"),sQuery(id+"F18.wireOp",EDGE,"E135"),sQuery(id+"F18.wireOp",EDGE,"E136.filletArc"),sQuery(id+"F18.wireOp",EDGE,"E137.filletArc"),sQuery(id+"F18.wireOp",EDGE,"E138.filletArc"),sQuery(id+"F18.wireOp",EDGE,"E139.filletArc"),sQuery(id+"F18.wireOp",EDGE,"E140"),sQuery(id+"F18.wireOp",EDGE,"E141"),sQuery(id+"F18.wireOp",EDGE,"E142"),sQuery(id+"F18.wireOp",EDGE,"E143.trimOffspring"),sQuery(id+"F18.wireOp",EDGE,"E144.filletArc"),sQuery(id+"F18.wireOp",EDGE,"E145.filletArc")])],"isStart":true});
            var sketch = newSketch(context, id + "F20", { "sketchPlane" : qUnion([Q0])});
            skLineSegment(sketch, "E146", {"start": v(-31.4, 143.18) * mm, "end": v(-44.12, 155.9) * mm});
            skLineSegment(sketch, "E147", {"start": v(-44.12, 155.9) * mm, "end": v(-42.21, 157.82) * mm});
            skLineSegment(sketch, "E148", {"start": v(-42.21, 157.82) * mm, "end": v(-29.48, 145.09) * mm});
            skLineSegment(sketch, "E149", {"start": v(-29.48, 145.09) * mm, "end": v(-31.4, 143.18) * mm});
            skSolve(sketch);
        }
        {
            var Q0;
            Q0=makeQuery(id+"F20.imprint","IMPRINT",FACE,{"disambiguationData":[TD([[makeQuery(id+"F20.imprint","IMPRINT",EDGE,{"derivedFrom":sQuery(id+"F20.wireOp",EDGE,"E146")}),1.0]])]});
            extrude(context, id + "F21", {"entities" : qUnion([Q0]), "operationType" : NewBodyOperationType.ADD, "depth" : 10 * mm});
        }
        {
            var Q0;
            Q0=makeQuery(id+"F21.boolean.opBoolean","MERGE",FACE,{"derivedFrom":[makeQuery(id+"F19.opExtrude","SWEPT_FACE",FACE,{"disambiguationData":[OSD([sQuery(id+"F18.wireOp",EDGE,"E127")])]}),makeQuery(id+"F21.opExtrude","SWEPT_FACE",FACE,{"disambiguationData":[OSD([sQuery(id+"F20.wireOp",EDGE,"E146")])]})]});
            var sketch = newSketch(context, id + "F22", { "sketchPlane" : qUnion([Q0])});
            skLineSegment(sketch, "E150", {"start": v(0, 135.44) * mm, "end": v(-6, 135.44) * mm, "construction": true});
            skCircle(sketch, "E151", {"center": v(-6, 135.44) * mm, "radius": 2.2 * mm});
            skCircle(sketch, "E152", {"center": v(-6, 135.44) * mm, "radius": 3 * mm});
            skSolve(sketch);
        }
        {
            var Q0;
            Q0=makeQuery(id+"F22.imprint","IMPRINT",FACE,{"disambiguationData":[TD([[makeQuery(id+"F22.imprint","IMPRINT",EDGE,{"derivedFrom":sQuery(id+"F22.wireOp",EDGE,"E151")}),1.0]])]});
            extrude(context, id + "F23", {"entities" : qUnion([Q0]), "operationType" : NewBodyOperationType.REMOVE, "endBound" : BoundingType.UP_TO_NEXT, "oppositeDirection" : true, "depth" : 25 * mm});
        }
        {
            var Q0;
            Q0=makeQuery(id+"F22.imprint","IMPRINT",FACE,{"disambiguationData":[TD([[makeQuery(id+"F22.imprint","IMPRINT",EDGE,{"derivedFrom":sQuery(id+"F22.wireOp",EDGE,"E151")}),-1.0]])]});
            var Q1;
            Q1=makeQuery(id+"F22.imprint","IMPRINT",FACE,{"disambiguationData":[TD([[makeQuery(id+"F22.imprint","IMPRINT",EDGE,{"derivedFrom":sQuery(id+"F22.wireOp",EDGE,"E151")}),1.0]])]});
            var Q2;
            Q2=sQuery(id+"F22.wireOp",EDGE,"E152");
            extrude(context, id + "F24", {"entities" : qUnion([Q0, Q1]), "operationType" : NewBodyOperationType.REMOVE, "surfaceEntities" : qUnion([Q2]), "oppositeDirection" : true, "depth" : 0.8 * mm});
        }
        {
            var Q0;
            Q0=makeQuery(id+"F19.opExtrude","CAP_EDGE",EDGE,{"disambiguationData":[OSD([sQuery(id+"F18.wireOp",EDGE,"E126")])],"isStart":false});
            var Q1;
            Q1=makeQuery(id+"F21.opExtrude","CAP_EDGE",EDGE,{"disambiguationData":[OSD([sQuery(id+"F20.wireOp",EDGE,"E149")])],"isStart":false});
            fillet(context, id + "F25", {"entities" : qUnion([Q0, Q1]), "radius" : 7 * mm, "tangentPropagation" : true, "allowEdgeOverflow" : false});
        }
        {
            var Q0;
            Q0=makeQuery(id+"F21.opExtrude","CAP_EDGE",EDGE,{"disambiguationData":[OSD([sQuery(id+"F20.wireOp",EDGE,"E147")])],"isStart":false});
            var Q1;
            Q1=makeQuery(id+"F19.opExtrude","SWEPT_EDGE",EDGE,{"disambiguationData":[OSD([sQuery(id+"F18.wireOp",EDGE,"E121"),sQuery(id+"F18.wireOp",EDGE,"E125")])]});
            fillet(context, id + "F26", {"entities" : qUnion([Q0, Q1]), "radius" : 3 * mm, "tangentPropagation" : true, "allowEdgeOverflow" : false});
        }
        {
            var Q0;
            Q0=makeQuery(id+"F21.boolean.opBoolean","MERGE",EDGE,{"derivedFrom":[makeQuery(id+"F19.opExtrude","SWEPT_EDGE",EDGE,{"disambiguationData":[OSD([sQuery(id+"F18.wireOp",EDGE,"E127"),sQuery(id+"F18.wireOp",EDGE,"E129")])]}),makeQuery(id+"F21.opExtrude","SWEPT_EDGE",EDGE,{"disambiguationData":[OSD([sQuery(id+"F20.wireOp",EDGE,"E146"),sQuery(id+"F20.wireOp",EDGE,"E149")])]})]});
            fillet(context, id + "F27", {"entities" : qUnion([Q0]), "radius" : 7 * mm, "allowEdgeOverflow" : false});
        }
        {
            var Q0;
            Q0=makeQuery(id+"F27.opFillet","BLEND_EDGE",EDGE,{"blendedFrom":[makeQuery(id+"F21.boolean.opBoolean","MERGE",EDGE,{"derivedFrom":[makeQuery(id+"F19.opExtrude","SWEPT_EDGE",EDGE,{"disambiguationData":[OSD([sQuery(id+"F18.wireOp",EDGE,"E127"),sQuery(id+"F18.wireOp",EDGE,"E129")])]}),makeQuery(id+"F21.opExtrude","SWEPT_EDGE",EDGE,{"disambiguationData":[OSD([sQuery(id+"F20.wireOp",EDGE,"E146"),sQuery(id+"F20.wireOp",EDGE,"E149")])]})]}),makeQuery(id+"F21.boolean.opBoolean","MERGE",FACE,{"derivedFrom":[makeQuery(id+"F19.opExtrude","SWEPT_FACE",FACE,{"disambiguationData":[OSD([sQuery(id+"F18.wireOp",EDGE,"E125")])]}),makeQuery(id+"F21.opExtrude","SWEPT_FACE",FACE,{"disambiguationData":[OSD([sQuery(id+"F20.wireOp",EDGE,"E148")])]})]})],"blendedInto":[makeQuery(id+"F21.boolean.opBoolean","MERGE",FACE,{"derivedFrom":[makeQuery(id+"F19.opExtrude","SWEPT_FACE",FACE,{"disambiguationData":[OSD([sQuery(id+"F18.wireOp",EDGE,"E125")])]}),makeQuery(id+"F21.opExtrude","SWEPT_FACE",FACE,{"disambiguationData":[OSD([sQuery(id+"F20.wireOp",EDGE,"E148")])]})]})]});
            fillet(context, id + "F28", {"entities" : qUnion([Q0]), "radius" : 1 * mm, "tangentPropagation" : true, "allowEdgeOverflow" : false});
        }
        {
            var Q0;
            Q0=makeQuery(id+"F19.opExtrude","CAP_FACE",FACE,{"disambiguationData":[OSD([sQuery(id+"F18.wireOp",EDGE,"E120"),sQuery(id+"F18.wireOp",EDGE,"E121"),sQuery(id+"F18.wireOp",EDGE,"E122"),sQuery(id+"F18.wireOp",EDGE,"E123"),sQuery(id+"F18.wireOp",EDGE,"E125"),sQuery(id+"F18.wireOp",EDGE,"E126"),sQuery(id+"F18.wireOp",EDGE,"E127"),sQuery(id+"F18.wireOp",EDGE,"E128"),sQuery(id+"F18.wireOp",EDGE,"E129"),sQuery(id+"F18.wireOp",EDGE,"E130"),sQuery(id+"F18.wireOp",EDGE,"E131"),sQuery(id+"F18.wireOp",EDGE,"E132"),sQuery(id+"F18.wireOp",EDGE,"E133"),sQuery(id+"F18.wireOp",EDGE,"E134"),sQuery(id+"F18.wireOp",EDGE,"E135"),sQuery(id+"F18.wireOp",EDGE,"E136.filletArc"),sQuery(id+"F18.wireOp",EDGE,"E137.filletArc"),sQuery(id+"F18.wireOp",EDGE,"E138.filletArc"),sQuery(id+"F18.wireOp",EDGE,"E139.filletArc"),sQuery(id+"F18.wireOp",EDGE,"E140"),sQuery(id+"F18.wireOp",EDGE,"E141"),sQuery(id+"F18.wireOp",EDGE,"E142"),sQuery(id+"F18.wireOp",EDGE,"E143.trimOffspring"),sQuery(id+"F18.wireOp",EDGE,"E144.filletArc"),sQuery(id+"F18.wireOp",EDGE,"E145.filletArc")])],"isStart":false});
            var sketch = newSketch(context, id + "F29", { "sketchPlane" : qUnion([Q0])});
            skCircle(sketch, "E153", {"center": v(6, 191) * mm, "radius": 3 * mm});
            skCircle(sketch, "E154", {"center": v(6, 173) * mm, "radius": 3 * mm});
            skArc(sketch, "E155", {"start": v(22.9, 164.4) * mm, "mid": v(18.67, 164.4) * mm, "end": v(18.67, 160.15) * mm});
            skArc(sketch, "E156", {"start": v(27.15, 151.67) * mm, "mid": v(31.4, 151.67) * mm, "end": v(31.4, 155.9) * mm});
            skLineSegment(sketch, "E157", {"start": v(22.9, 164.4) * mm, "end": v(31.4, 155.9) * mm});
            skLineSegment(sketch, "E158", {"start": v(27.15, 151.67) * mm, "end": v(18.67, 160.15) * mm});
            skSolve(sketch);
        }
        {
            var Q0;
            Q0=qSketchRegion(id+"F29",true);
            extrude(context, id + "F30", {"entities" : qUnion([Q0]), "operationType" : NewBodyOperationType.REMOVE, "oppositeDirection" : true, "depth" : 1 * mm});
        }
        {
            var Q0;
            Q0=makeQuery(id+"F19.opExtrude","CAP_EDGE",EDGE,{"disambiguationData":[OSD([sQuery(id+"F18.wireOp",EDGE,"E120")])],"isStart":false});
            chamfer(context, id + "F31", {"entities" : qUnion([Q0]), "width" : 2 * mm});
        }
        {
            var Q0;
            Q0=makeQuery(id+"F19.opExtrude","SWEPT_BODY",BODY,{"disambiguationData":[OSD([sQuery(id+"F18.wireOp",EDGE,"E120"),sQuery(id+"F18.wireOp",EDGE,"E121"),sQuery(id+"F18.wireOp",EDGE,"E122"),sQuery(id+"F18.wireOp",EDGE,"E123"),sQuery(id+"F18.wireOp",EDGE,"E125"),sQuery(id+"F18.wireOp",EDGE,"E126"),sQuery(id+"F18.wireOp",EDGE,"E127"),sQuery(id+"F18.wireOp",EDGE,"E128"),sQuery(id+"F18.wireOp",EDGE,"E129"),sQuery(id+"F18.wireOp",EDGE,"E130"),sQuery(id+"F18.wireOp",EDGE,"E131"),sQuery(id+"F18.wireOp",EDGE,"E132"),sQuery(id+"F18.wireOp",EDGE,"E133"),sQuery(id+"F18.wireOp",EDGE,"E134"),sQuery(id+"F18.wireOp",EDGE,"E135"),sQuery(id+"F18.wireOp",EDGE,"E136.filletArc"),sQuery(id+"F18.wireOp",EDGE,"E137.filletArc"),sQuery(id+"F18.wireOp",EDGE,"E138.filletArc"),sQuery(id+"F18.wireOp",EDGE,"E139.filletArc"),sQuery(id+"F18.wireOp",EDGE,"E140"),sQuery(id+"F18.wireOp",EDGE,"E141"),sQuery(id+"F18.wireOp",EDGE,"E142"),sQuery(id+"F18.wireOp",EDGE,"E143.trimOffspring"),sQuery(id+"F18.wireOp",EDGE,"E144.filletArc"),sQuery(id+"F18.wireOp",EDGE,"E145.filletArc")])]});
            var Q1;
            Q1=qCreatedBy(makeId("Right.planeOp"),FACE);
            mirror(context, id + "F32", {"entities" : qUnion([Q0]), "mirrorPlane" : qUnion([Q1])});
        }
    });
